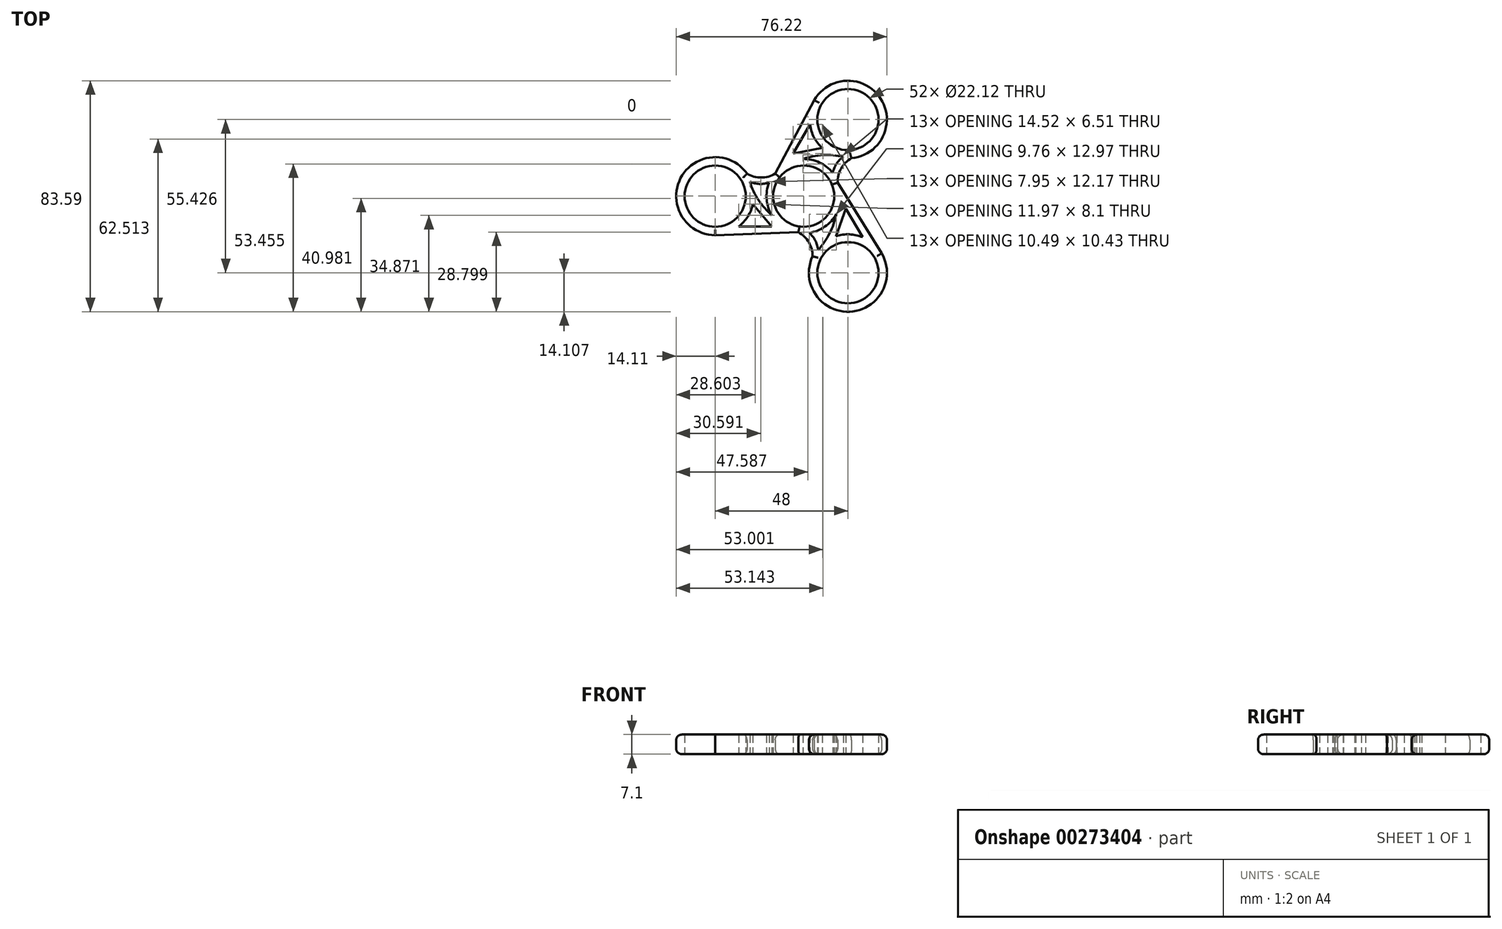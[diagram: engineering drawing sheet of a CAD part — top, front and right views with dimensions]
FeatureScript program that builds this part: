
annotation { "Feature Type Name" : "Feature", "Feature Type Description" : "" }
export const myFeature = defineFeature(function(context is Context, id is Id, definition is map)
    precondition{}
    {
        {
            var Q0;
            Q0=qCreatedBy(makeId("Top.planeOp"),FACE);
            var sketch = newSketch(context, id + "F0", { "sketchPlane" : qUnion([Q0])});
            skCircle(sketch, "E0", {"center": v(0, 0) * mm, "radius": 11.06 * mm});
            skCircle(sketch, "E1", {"center": v(16, 27.71) * mm, "radius": 11.06 * mm});
            skLineSegment(sketch, "E2", {"start": v(0, 0) * mm, "end": v(16, 27.71) * mm, "construction": true});
            skArc(sketch, "E3", {"start": v(17.28, 13.71) * mm, "mid": v(27.84, 35.3) * mm, "end": v(3.82, 34.74) * mm});
            skPoint(sketch, "E4.visualSharp", {"position": v(8.97, 15.54) * mm});
            skLineSegment(sketch, "E5", {"start": v(8, 13.86) * mm, "end": v(-1.53, 19.36) * mm, "construction": true});
            skArc(sketch, "E6", {"start": v(2.26, 25.91) * mm, "mid": v(3.73, 21.27) * mm, "end": v(6.72, 17.42) * mm});
            skLineSegment(sketch, "E7", {"start": v(-1.53, 19.36) * mm, "end": v(-3.77, 15.48) * mm});
            skLineSegment(sketch, "E8", {"start": v(-1.53, 19.36) * mm, "end": v(2.26, 25.91) * mm});
            skLineSegment(sketch, "E9", {"start": v(12.33, 11.36) * mm, "end": v(15.1, 14.15) * mm, "construction": true});
            skLineSegment(sketch, "E10", {"start": v(12.33, 11.36) * mm, "end": v(10.43, 8.07) * mm, "construction": true});
            skPoint(sketch, "E11.center", {"position": v(-0.23, 0.06) * mm});
            skLineSegment(sketch, "E12", {"start": v(6.72, 17.42) * mm, "end": v(-3.77, 15.48) * mm});
            skPoint(sketch, "E13.orphan", {"position": v(9.2, 15.94) * mm});
            skPoint(sketch, "E14.2.12", {"position": v(12.73, -0.04) * mm});
            skPoint(sketch, "E14.2.17", {"position": v(14.65, -3.37) * mm});
            skPoint(sketch, "E15.visualSharp", {"position": v(11.85, 5.8) * mm});
            skArc(sketch, "E16", {"start": v(17.28, 13.71) * mm, "mid": v(13.53, 9.98) * mm, "end": v(12.27, 4.84) * mm});
            skArc(sketch, "E17", {"start": v(14.3, 14.26) * mm, "mid": v(11.76, 11.54) * mm, "end": v(10.43, 8.07) * mm});
            skArc(sketch, "E18.2.0", {"start": v(14.3, 14.26) * mm, "mid": v(6.98, 14.85) * mm, "end": v(-0.22, 13.46) * mm});
            skArc(sketch, "E18.2.1", {"start": v(10.5, 8.38) * mm, "mid": v(4.7, 12.6) * mm, "end": v(-2.45, 13.25) * mm});
            skPoint(sketch, "E19.1.1", {"position": v(-10.95, 7.36) * mm});
            skPoint(sketch, "E19.1.2", {"position": v(-17.9, 0) * mm});
            skCircle(sketch, "E19.1.3", {"center": v(-32, 0) * mm, "radius": 11.06 * mm});
            skArc(sketch, "E19.1.4", {"start": v(-20.48, 8.13) * mm, "mid": v(-44.52, 6.49) * mm, "end": v(-32, -14.1) * mm});
            skLineSegment(sketch, "E19.1.5", {"start": v(-16, 0) * mm, "end": v(-16, -11) * mm, "construction": true});
            skArc(sketch, "E19.1.6", {"start": v(-12.5, 4.9) * mm, "mid": v(-13.26, -2.24) * mm, "end": v(-10.25, -8.75) * mm});
            skLineSegment(sketch, "E19.1.7", {"start": v(-18.4, -2.9) * mm, "end": v(-11.52, -11) * mm});
            skPoint(sketch, "E19.1.8", {"position": v(-18.4, 0) * mm});
            skArc(sketch, "E19.1.10", {"start": v(-19.5, 5.25) * mm, "mid": v(-16.35, -1.38) * mm, "end": v(-11.55, -6.92) * mm});
            skArc(sketch, "E19.1.11", {"start": v(-23.5, -11) * mm, "mid": v(-20.23, -7.4) * mm, "end": v(-18.4, -2.9) * mm});
            skArc(sketch, "E19.1.13", {"start": v(-20.48, 8.13) * mm, "mid": v(-15.37, 6.73) * mm, "end": v(-10.29, 8.18) * mm});
            skLineSegment(sketch, "E19.1.14", {"start": v(-16, -11) * mm, "end": v(-11.52, -11) * mm});
            skLineSegment(sketch, "E19.1.15", {"start": v(-16, -11) * mm, "end": v(-23.5, -11) * mm});
            skArc(sketch, "E19.1.16", {"start": v(-19.5, 5.25) * mm, "mid": v(-15.87, 4.42) * mm, "end": v(-12.2, 5) * mm});
            skLineSegment(sketch, "E19.1.17", {"start": v(-16, 5) * mm, "end": v(-12.2, 5) * mm, "construction": true});
            skLineSegment(sketch, "E19.1.18", {"start": v(-16, 5) * mm, "end": v(-19.8, 6) * mm, "construction": true});
            skPoint(sketch, "E19.2.1", {"position": v(-0.9, -13.16) * mm});
            skPoint(sketch, "E19.2.2", {"position": v(8.95, -15.5) * mm});
            skCircle(sketch, "E19.2.3", {"center": v(16, -27.71) * mm, "radius": 11.06 * mm});
            skArc(sketch, "E19.2.4", {"start": v(3.2, -21.8) * mm, "mid": v(16.64, -41.8) * mm, "end": v(28.22, -20.66) * mm});
            skLineSegment(sketch, "E19.2.5", {"start": v(8, -13.86) * mm, "end": v(17.53, -8.36) * mm, "construction": true});
            skArc(sketch, "E19.2.6", {"start": v(2.01, -13.28) * mm, "mid": v(8.57, -10.36) * mm, "end": v(12.7, -4.5) * mm});
            skLineSegment(sketch, "E19.2.7", {"start": v(11.71, -14.49) * mm, "end": v(15.29, -4.48) * mm});
            skPoint(sketch, "E19.2.8", {"position": v(9.2, -15.94) * mm});
            skArc(sketch, "E19.2.10", {"start": v(5.2, -19.5) * mm, "mid": v(9.37, -13.47) * mm, "end": v(11.77, -6.54) * mm});
            skArc(sketch, "E19.2.11", {"start": v(21.27, -14.85) * mm, "mid": v(16.52, -13.82) * mm, "end": v(11.71, -14.49) * mm});
            skArc(sketch, "E19.2.13", {"start": v(3.2, -21.8) * mm, "mid": v(1.85, -16.7) * mm, "end": v(-1.94, -13.04) * mm});
            skLineSegment(sketch, "E19.2.14", {"start": v(17.53, -8.36) * mm, "end": v(15.29, -4.48) * mm});
            skLineSegment(sketch, "E19.2.15", {"start": v(17.53, -8.36) * mm, "end": v(21.27, -14.85) * mm});
            skArc(sketch, "E19.2.16", {"start": v(5.2, -19.5) * mm, "mid": v(4.11, -15.95) * mm, "end": v(1.77, -13.07) * mm});
            skLineSegment(sketch, "E19.2.17", {"start": v(3.67, -16.36) * mm, "end": v(1.77, -13.07) * mm, "construction": true});
            skLineSegment(sketch, "E19.2.18", {"start": v(3.67, -16.36) * mm, "end": v(4.7, -20.15) * mm, "construction": true});
            skLineSegment(sketch, "E20", {"start": v(-10.29, 8.18) * mm, "end": v(3.82, 34.74) * mm});
            skLineSegment(sketch, "E21", {"start": v(12.27, 4.84) * mm, "end": v(28.22, -20.66) * mm});
            skLineSegment(sketch, "E22", {"start": v(-32, -14.1) * mm, "end": v(-1.94, -13.04) * mm});
            skSolve(sketch);
        }
        {
            var Q0;
            Q0=makeQuery(id+"F0.imprint","IMPRINT",FACE,{"disambiguationData":[TD([[makeQuery(id+"F0.imprint","IMPRINT",EDGE,{"derivedFrom":sQuery(id+"F0.wireOp",EDGE,"ea44153e-c5e4-4200-878d-53ebf284e07f.1.0")}),-1.0]])]});
            var Q1;
            Q1=makeQuery(id+"F0.imprint","IMPRINT",FACE,{"disambiguationData":[TD([[makeQuery(id+"F0.imprint","IMPRINT",EDGE,{"derivedFrom":sQuery(id+"F0.wireOp",EDGE,"E0")}),-1.0]])]});
            var Q2;
            Q2=makeQuery(id+"F0.imprint","IMPRINT",FACE,{"disambiguationData":[TD([[makeQuery(id+"F0.imprint","IMPRINT",EDGE,{"derivedFrom":sQuery(id+"F0.wireOp",EDGE,"E1")}),-1.0]])]});
            var Q3;
            {var subQ0=sQuery(id+"F0.wireOp",EDGE,"zqQpl2xC-KShR-byGl-JfGq-b1LpVGurQPJH");Q3=makeQuery(id+"F0.imprint","IMPRINT",FACE,{"disambiguationData":[TD([[makeQuery(id+"F0.imprint","IMPRINT",EDGE,{"derivedFrom":subQ0}),-1.0]])]});}
            extrude(context, id + "F1", {"entities" : qUnion([Q0, Q1, Q2, Q3]), "depth" : 7.1 * mm});
        }
        {
            var Q0;
            Q0=makeQuery(id+"F1.opExtrude","CAP_EDGE",EDGE,{"disambiguationData":[OSD([sQuery(id+"F0.wireOp",EDGE,"9da3e264-2dd3-4d40-bf33-df63ea0aea25.2.1")])],"isStart":false});
            var Q1;
            Q1=makeQuery(id+"F1.opExtrude","CAP_EDGE",EDGE,{"disambiguationData":[OSD([sQuery(id+"F0.wireOp",EDGE,"E14.1.16")])],"isStart":false});
            var Q2;
            Q2=makeQuery(id+"F1.opExtrude","CAP_EDGE",EDGE,{"disambiguationData":[OSD([sQuery(id+"F0.wireOp",EDGE,"9da3e264-2dd3-4d40-bf33-df63ea0aea25.1.0")])],"isStart":false});
            var Q3;
            Q3=makeQuery(id+"F1.opExtrude","CAP_EDGE",EDGE,{"disambiguationData":[OSD([sQuery(id+"F0.wireOp",EDGE,"9da3e264-2dd3-4d40-bf33-df63ea0aea25.1.1")])],"isStart":false});
            var Q4;
            Q4=makeQuery(id+"F1.opExtrude","CAP_EDGE",EDGE,{"disambiguationData":[OSD([sQuery(id+"F0.wireOp",EDGE,"E3")])],"isStart":false});
            var Q5;
            Q5=makeQuery(id+"F1.opExtrude","CAP_EDGE",EDGE,{"disambiguationData":[OSD([sQuery(id+"F0.wireOp",EDGE,"E16")])],"isStart":false});
            var Q6;
            Q6=makeQuery(id+"F1.opExtrude","CAP_EDGE",EDGE,{"disambiguationData":[OSD([sQuery(id+"F0.wireOp",EDGE,"6a0h13Az-n91s-kYTk-ymzQ-JrsRaVEbtbDH")])],"isStart":false});
            var Q7;
            Q7=makeQuery(id+"F1.opExtrude","CAP_EDGE",EDGE,{"disambiguationData":[OSD([sQuery(id+"F0.wireOp",EDGE,"E14.2.16")])],"isStart":false});
            var Q8;
            Q8=makeQuery(id+"F1.opExtrude","CAP_EDGE",EDGE,{"disambiguationData":[OSD([sQuery(id+"F0.wireOp",EDGE,"9da3e264-2dd3-4d40-bf33-df63ea0aea25.2.0")])],"isStart":false});
            var Q9;
            Q9=makeQuery(id+"F1.opExtrude","CAP_EDGE",EDGE,{"disambiguationData":[OSD([sQuery(id+"F0.wireOp",EDGE,"E14.1.16")])],"isStart":true});
            var Q10;
            Q10=makeQuery(id+"F1.opExtrude","CAP_EDGE",EDGE,{"disambiguationData":[OSD([sQuery(id+"F0.wireOp",EDGE,"9da3e264-2dd3-4d40-bf33-df63ea0aea25.2.1")])],"isStart":true});
            var Q11;
            Q11=makeQuery(id+"F1.opExtrude","CAP_EDGE",EDGE,{"disambiguationData":[OSD([sQuery(id+"F0.wireOp",EDGE,"9da3e264-2dd3-4d40-bf33-df63ea0aea25.2.0")])],"isStart":true});
            var Q12;
            Q12=makeQuery(id+"F1.opExtrude","CAP_EDGE",EDGE,{"disambiguationData":[OSD([sQuery(id+"F0.wireOp",EDGE,"E14.2.16")])],"isStart":true});
            var Q13;
            Q13=makeQuery(id+"F1.opExtrude","CAP_EDGE",EDGE,{"disambiguationData":[OSD([sQuery(id+"F0.wireOp",EDGE,"6a0h13Az-n91s-kYTk-ymzQ-JrsRaVEbtbDH")])],"isStart":true});
            var Q14;
            Q14=makeQuery(id+"F1.opExtrude","CAP_EDGE",EDGE,{"disambiguationData":[OSD([sQuery(id+"F0.wireOp",EDGE,"E16")])],"isStart":true});
            var Q15;
            Q15=makeQuery(id+"F1.opExtrude","CAP_EDGE",EDGE,{"disambiguationData":[OSD([sQuery(id+"F0.wireOp",EDGE,"9da3e264-2dd3-4d40-bf33-df63ea0aea25.1.1")])],"isStart":true});
            var Q16;
            Q16=makeQuery(id+"F1.opExtrude","CAP_EDGE",EDGE,{"disambiguationData":[OSD([sQuery(id+"F0.wireOp",EDGE,"E22")])],"isStart":false});
            var Q17;
            Q17=makeQuery(id+"F1.opExtrude","CAP_EDGE",EDGE,{"disambiguationData":[OSD([sQuery(id+"F0.wireOp",EDGE,"E21")])],"isStart":false});
            var Q18;
            Q18=makeQuery(id+"F1.opExtrude","CAP_EDGE",EDGE,{"disambiguationData":[OSD([sQuery(id+"F0.wireOp",EDGE,"E19.2.4")])],"isStart":false});
            var Q19;
            Q19=makeQuery(id+"F1.opExtrude","CAP_EDGE",EDGE,{"disambiguationData":[OSD([sQuery(id+"F0.wireOp",EDGE,"E19.1.4")])],"isStart":false});
            var Q20;
            Q20=makeQuery(id+"F1.opExtrude","CAP_EDGE",EDGE,{"disambiguationData":[OSD([sQuery(id+"F0.wireOp",EDGE,"E20")])],"isStart":false});
            var Q21;
            Q21=makeQuery(id+"F1.opExtrude","CAP_EDGE",EDGE,{"disambiguationData":[OSD([sQuery(id+"F0.wireOp",EDGE,"E19.1.13")])],"isStart":false});
            var Q22;
            Q22=makeQuery(id+"F1.opExtrude","CAP_EDGE",EDGE,{"disambiguationData":[OSD([sQuery(id+"F0.wireOp",EDGE,"E19.2.13")])],"isStart":false});
            var Q23;
            Q23=makeQuery(id+"F1.opExtrude","CAP_EDGE",EDGE,{"disambiguationData":[OSD([sQuery(id+"F0.wireOp",EDGE,"E22")])],"isStart":true});
            var Q24;
            Q24=makeQuery(id+"F1.opExtrude","CAP_EDGE",EDGE,{"disambiguationData":[OSD([sQuery(id+"F0.wireOp",EDGE,"E19.2.13")])],"isStart":true});
            var Q25;
            Q25=makeQuery(id+"F1.opExtrude","CAP_EDGE",EDGE,{"disambiguationData":[OSD([sQuery(id+"F0.wireOp",EDGE,"E19.2.4")])],"isStart":true});
            var Q26;
            Q26=makeQuery(id+"F1.opExtrude","CAP_EDGE",EDGE,{"disambiguationData":[OSD([sQuery(id+"F0.wireOp",EDGE,"E19.1.4")])],"isStart":true});
            var Q27;
            Q27=makeQuery(id+"F1.opExtrude","CAP_EDGE",EDGE,{"disambiguationData":[OSD([sQuery(id+"F0.wireOp",EDGE,"E20")])],"isStart":true});
            var Q28;
            Q28=makeQuery(id+"F1.opExtrude","CAP_EDGE",EDGE,{"disambiguationData":[OSD([sQuery(id+"F0.wireOp",EDGE,"E19.1.13")])],"isStart":true});
            var Q29;
            Q29=makeQuery(id+"F1.opExtrude","CAP_EDGE",EDGE,{"disambiguationData":[OSD([sQuery(id+"F0.wireOp",EDGE,"E21")])],"isStart":true});
            var Q30;
            Q30=makeQuery(id+"F1.opExtrude","CAP_EDGE",EDGE,{"disambiguationData":[OSD([sQuery(id+"F0.wireOp",EDGE,"E3")])],"isStart":true});
            fillet(context, id + "F2", {"entities" : qUnion([Q0, Q1, Q2, Q3, Q4, Q5, Q6, Q7, Q8, Q9, Q10, Q11, Q12, Q13, Q14, Q15, Q16, Q17, Q18, Q19, Q20, Q21, Q22, Q23, Q24, Q25, Q26, Q27, Q28, Q29, Q30]), "radius" : 2 * mm, "tangentPropagation" : true, "allowEdgeOverflow" : false});
        }
    });
